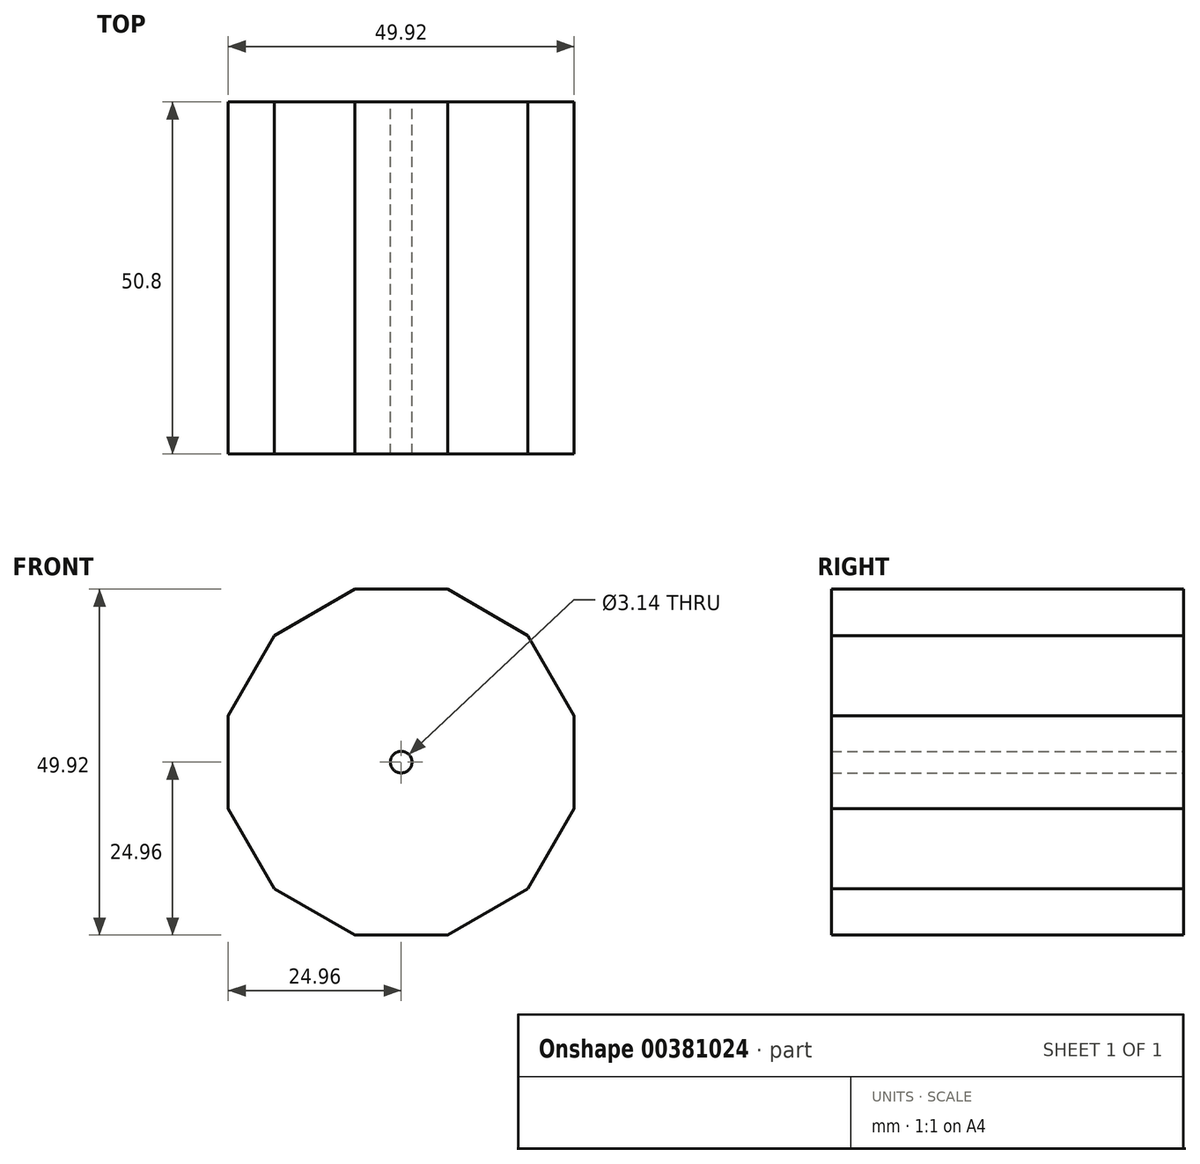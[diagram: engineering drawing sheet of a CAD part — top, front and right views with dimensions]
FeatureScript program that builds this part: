
annotation { "Feature Type Name" : "Feature", "Feature Type Description" : "" }
export const myFeature = defineFeature(function(context is Context, id is Id, definition is map)
    precondition{}
    {
        {
            var Q0;
            Q0=qCreatedBy(makeId("Front.planeOp"),FACE);
            var sketch = newSketch(context, id + "F0", { "sketchPlane" : qUnion([Q0])});
            skCircle(sketch, "E0.cCircle", {"center": v(0, 0) * mm, "radius": 24.96 * mm, "construction": true});
            skLineSegment(sketch, "E0.0", {"start": v(-6.69, 24.96) * mm, "end": v(6.69, 24.96) * mm});
            skLineSegment(sketch, "E0.1", {"start": v(6.69, 24.96) * mm, "end": v(18.27, 18.27) * mm});
            skLineSegment(sketch, "E0.2", {"start": v(18.27, 18.27) * mm, "end": v(24.96, 6.69) * mm});
            skLineSegment(sketch, "E0.3", {"start": v(24.96, 6.69) * mm, "end": v(24.96, -6.69) * mm});
            skLineSegment(sketch, "E0.4", {"start": v(24.96, -6.69) * mm, "end": v(18.27, -18.27) * mm});
            skLineSegment(sketch, "E0.5", {"start": v(18.27, -18.27) * mm, "end": v(6.69, -24.96) * mm});
            skLineSegment(sketch, "E0.6", {"start": v(6.69, -24.96) * mm, "end": v(-6.69, -24.96) * mm});
            skLineSegment(sketch, "E0.7", {"start": v(-6.69, -24.96) * mm, "end": v(-18.27, -18.27) * mm});
            skLineSegment(sketch, "E0.8", {"start": v(-18.27, -18.27) * mm, "end": v(-24.96, -6.69) * mm});
            skLineSegment(sketch, "E0.9", {"start": v(-24.96, -6.69) * mm, "end": v(-24.96, 6.69) * mm});
            skLineSegment(sketch, "E0.10", {"start": v(-24.96, 6.69) * mm, "end": v(-18.27, 18.27) * mm});
            skLineSegment(sketch, "E0.11", {"start": v(-18.27, 18.27) * mm, "end": v(-6.69, 24.96) * mm});
            skPoint(sketch, "E0.0.midPoint", {"position": v(0, 24.96) * mm});
            skCircle(sketch, "E1", {"center": v(0, 0) * mm, "radius": 1.57 * mm});
            skSolve(sketch);
        }
        {
            var Q0;
            Q0=makeQuery(id+"F0.imprint","IMPRINT",FACE,{"disambiguationData":[TD([[makeQuery(id+"F0.imprint","IMPRINT",EDGE,{"derivedFrom":sQuery(id+"F0.wireOp",EDGE,"6c9d56e5-fcf1-41b7-9989-5857b26e0291.0")}),-1.0]])]});
            var Q1;
            Q1=makeQuery(id+"F0.imprint","IMPRINT",FACE,{"disambiguationData":[TD([[makeQuery(id+"F0.imprint","IMPRINT",EDGE,{"derivedFrom":sQuery(id+"F0.wireOp",EDGE,"E0.0")}),-1.0]])]});
            extrude(context, id + "F1", {"entities" : qUnion([Q0, Q1]), "depth" : 50.8 * mm});
        }
    });
